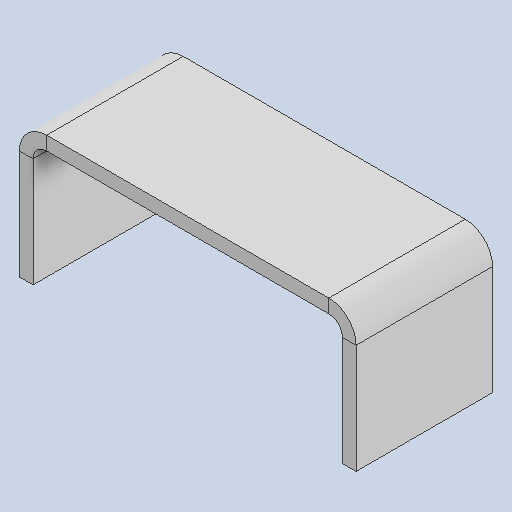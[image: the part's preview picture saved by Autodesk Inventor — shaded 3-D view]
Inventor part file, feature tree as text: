
AUTODESK INVENTOR PART (.ipt)
format: ipt  version: 2025 (Build 290162010, 162A)  size: 115,200 bytes
history: native  units: mm
features: sheet_metal_op x3, sketch x1, other x1
ambient origin geometry x8: Origin, YZ Plane, XZ Plane, XY Plane, X Axis, Y Axis, Z Axis, Center Point
bodies: Solid1 (feature_tree)
feature tree (5):
  sheet_metal_op  "Contour Flange1"
  sketch  "Sketch1"  dims[d0=30.0mm d1=74.0mm d4=3.0mm d5=3.0mm d6=1.5mm d7=6.0mm d8=3.0mm d9=30.0mm d10=3.0mm d11=3.048mm d12=12.0mm d13=3.0mm d14=3.0mm]
  other  "Plate1"
  sheet_metal_op  "Bend1"
  sheet_metal_op  "Corner1"
